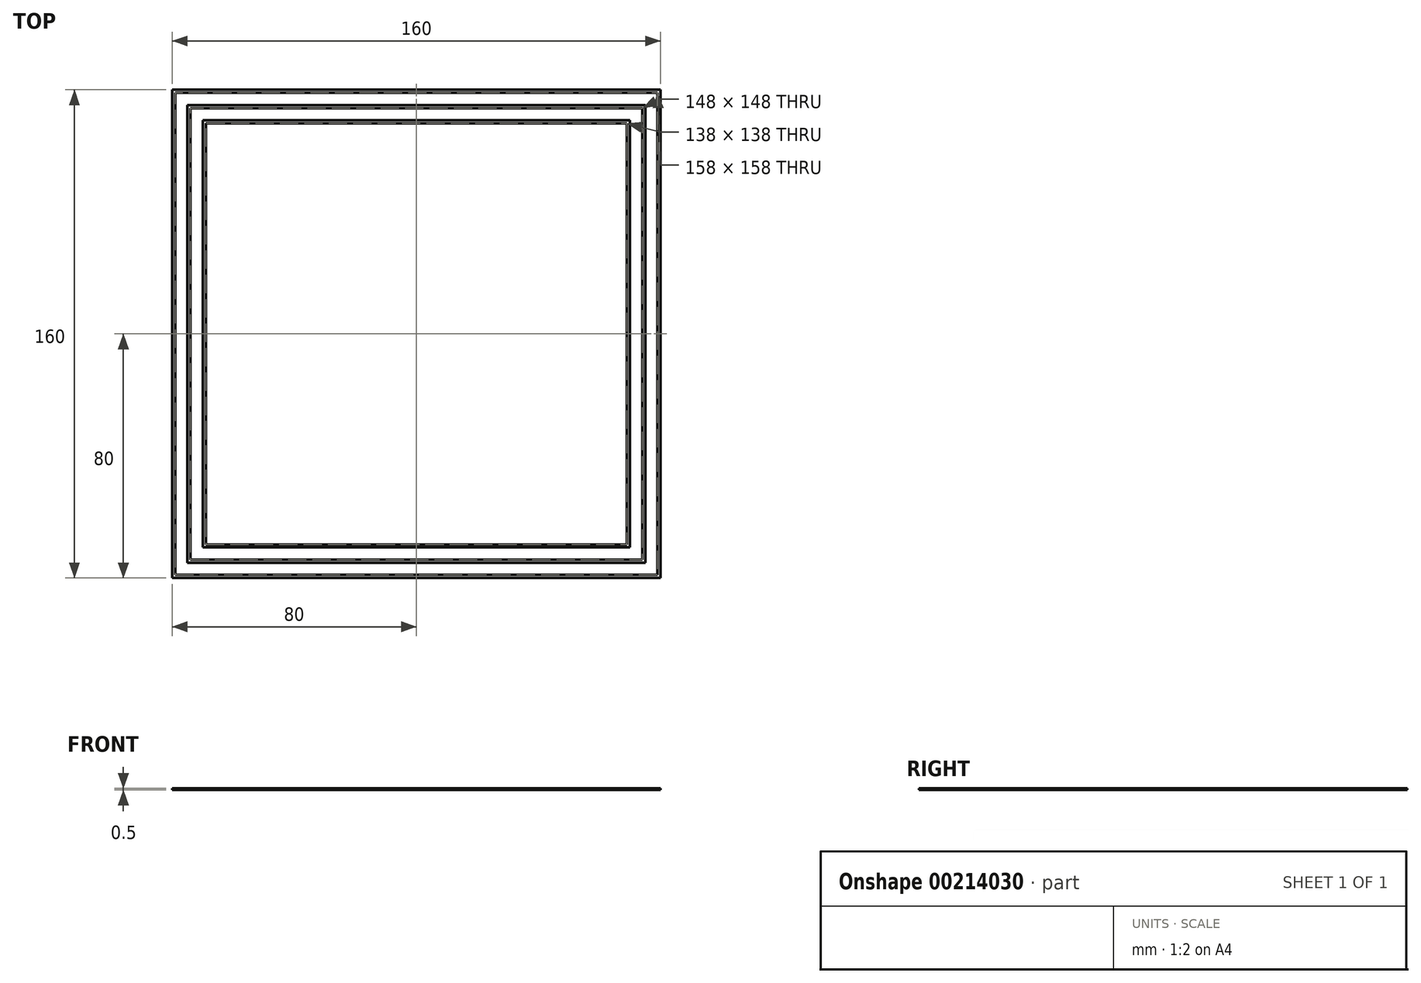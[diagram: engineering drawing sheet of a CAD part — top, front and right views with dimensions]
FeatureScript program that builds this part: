
annotation { "Feature Type Name" : "Feature", "Feature Type Description" : "" }
export const myFeature = defineFeature(function(context is Context, id is Id, definition is map)
    precondition{}
    {
        {
            var Q0;
            Q0=qCreatedBy(makeId("Top.planeOp"),FACE);
            var sketch = newSketch(context, id + "F0", { "sketchPlane" : qUnion([Q0])});
            skLineSegment(sketch, "E0.bottom", {"start": v(-80, 80) * mm, "end": v(80, 80) * mm});
            skLineSegment(sketch, "E0.top", {"start": v(-80, -80) * mm, "end": v(80, -80) * mm});
            skLineSegment(sketch, "E0.left", {"start": v(-80, 80) * mm, "end": v(-80, -80) * mm});
            skLineSegment(sketch, "E0.right", {"start": v(80, 80) * mm, "end": v(80, -80) * mm});
            skLineSegment(sketch, "E1.bottom", {"start": v(-79, 79) * mm, "end": v(79, 79) * mm});
            skLineSegment(sketch, "E1.top", {"start": v(-79, -79) * mm, "end": v(79, -79) * mm});
            skLineSegment(sketch, "E1.left", {"start": v(-79, 79) * mm, "end": v(-79, -79) * mm});
            skLineSegment(sketch, "E1.right", {"start": v(79, 79) * mm, "end": v(79, -79) * mm});
            skSolve(sketch);
        }
        {
            var Q0;
            Q0 = qSketchRegion(id + "F0", true);
            extrude(context, id + "F1", {"entities" : qUnion([Q0]), "depth" : 0.5 * mm});
        }
        {
            var Q0;
            Q0=qCreatedBy(makeId("Top.planeOp"),FACE);
            var sketch = newSketch(context, id + "F2", { "sketchPlane" : qUnion([Q0])});
            skLineSegment(sketch, "E2.bottom", {"start": v(-75, 75) * mm, "end": v(75, 75) * mm});
            skLineSegment(sketch, "E2.top", {"start": v(-75, -75) * mm, "end": v(75, -75) * mm});
            skLineSegment(sketch, "E2.left", {"start": v(-75, 75) * mm, "end": v(-75, -75) * mm});
            skLineSegment(sketch, "E2.right", {"start": v(75, 75) * mm, "end": v(75, -75) * mm});
            skLineSegment(sketch, "E3.bottom", {"start": v(-74, 74) * mm, "end": v(74, 74) * mm});
            skLineSegment(sketch, "E3.top", {"start": v(-74, -74) * mm, "end": v(74, -74) * mm});
            skLineSegment(sketch, "E3.left", {"start": v(-74, 74) * mm, "end": v(-74, -74) * mm});
            skLineSegment(sketch, "E3.right", {"start": v(74, 74) * mm, "end": v(74, -74) * mm});
            skSolve(sketch);
        }
        {
            var Q0;
            Q0=qCreatedBy(makeId("Top.planeOp"),FACE);
            var sketch = newSketch(context, id + "F3", { "sketchPlane" : qUnion([Q0])});
            skLineSegment(sketch, "E4.bottom", {"start": v(-70, 70) * mm, "end": v(70, 70) * mm});
            skLineSegment(sketch, "E4.top", {"start": v(-70, -70) * mm, "end": v(70, -70) * mm});
            skLineSegment(sketch, "E4.left", {"start": v(-70, 70) * mm, "end": v(-70, -70) * mm});
            skLineSegment(sketch, "E4.right", {"start": v(70, 70) * mm, "end": v(70, -70) * mm});
            skLineSegment(sketch, "E5.bottom", {"start": v(-69, 69) * mm, "end": v(69, 69) * mm});
            skLineSegment(sketch, "E5.top", {"start": v(-69, -69) * mm, "end": v(69, -69) * mm});
            skLineSegment(sketch, "E5.left", {"start": v(-69, 69) * mm, "end": v(-69, -69) * mm});
            skLineSegment(sketch, "E5.right", {"start": v(69, 69) * mm, "end": v(69, -69) * mm});
            skLineSegment(sketch, "E6.top", {"start": v(-79, -79) * mm, "end": v(79, -79) * mm});
            skSolve(sketch);
        }
        {
            var Q0;
            Q0 = qSketchRegion(id + "F2", true);
            extrude(context, id + "F4", {"entities" : qUnion([Q0]), "depth" : 0.5 * mm});
        }
        {
            var Q0;
            Q0 = qSketchRegion(id + "F3", true);
            extrude(context, id + "F5", {"entities" : qUnion([Q0]), "depth" : 0.5 * mm});
        }
    });
